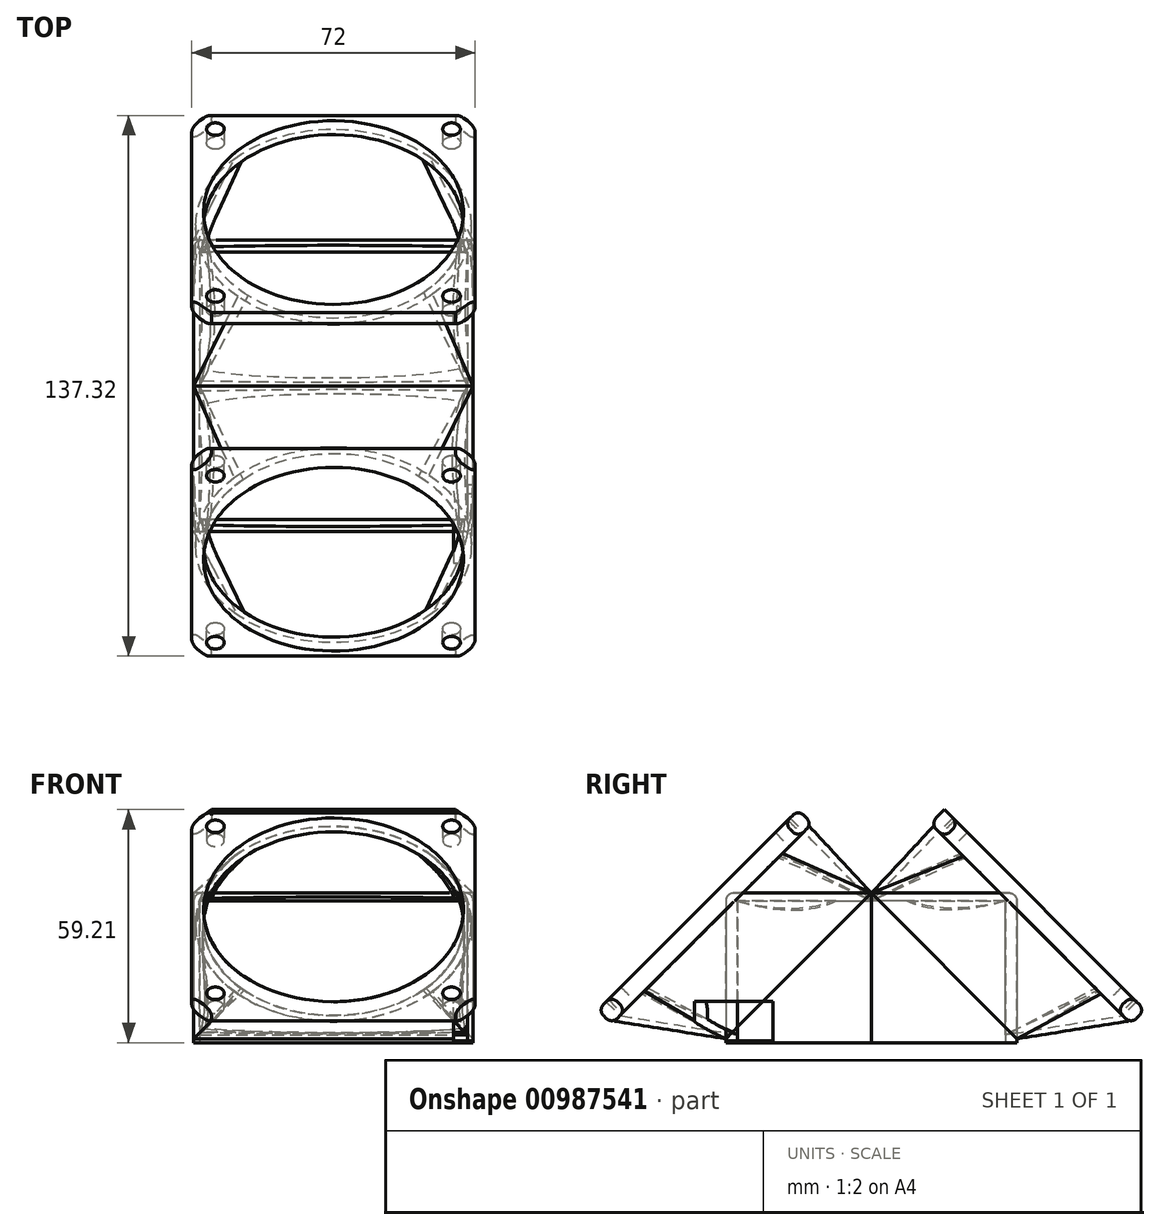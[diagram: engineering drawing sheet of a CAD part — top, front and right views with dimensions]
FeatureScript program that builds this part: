
annotation { "Feature Type Name" : "Feature", "Feature Type Description" : "" }
export const myFeature = defineFeature(function(context is Context, id is Id, definition is map)
    precondition{}
    {
        {
            var Q0;
            Q0=qCreatedBy(makeId("Front.planeOp"),FACE);
            var sketch = newSketch(context, id + "F0", { "sketchPlane" : qUnion([Q0])});
            skLineSegment(sketch, "E0.bottom", {"start": v(-34, 18) * mm, "end": v(34, 18) * mm});
            skLineSegment(sketch, "E0.top", {"start": v(-34, -18) * mm, "end": v(34, -18) * mm});
            skLineSegment(sketch, "E0.left", {"start": v(-34, 18) * mm, "end": v(-34, -18) * mm});
            skLineSegment(sketch, "E0.right", {"start": v(34, 18) * mm, "end": v(34, -18) * mm});
            skPoint(sketch, "E0.middle", {"position": v(0, 0) * mm});
            skSolve(sketch);
        }
        {
            var Q0;
            Q0=makeQuery(id+"F0.imprint","IMPRINT",FACE,{"disambiguationData":[TD([[makeQuery(id+"F0.imprint","IMPRINT",EDGE,{"derivedFrom":sQuery(id+"F0.wireOp",EDGE,"E0.bottom")}),-1.0]])]});
            extrude(context, id + "F1", {"entities" : qUnion([Q0]), "depth" : 34 * mm, "offsetDistance" : 25 * mm});
        }
        {
            var Q0;
            Q0=makeQuery(id+"F1.opExtrude","CAP_FACE",FACE,{"disambiguationData":[OSD([sQuery(id+"F0.wireOp",EDGE,"E0.bottom"),sQuery(id+"F0.wireOp",EDGE,"E0.top"),sQuery(id+"F0.wireOp",EDGE,"E0.left"),sQuery(id+"F0.wireOp",EDGE,"E0.right")])],"isStart":false});
            var sketch = newSketch(context, id + "F2", { "sketchPlane" : qUnion([Q0])});
            skLineSegment(sketch, "E1", {"start": v(-34, 0) * mm, "end": v(34, 0) * mm, "construction": true});
            skSolve(sketch);
        }
        {
            var Q0;
            Q0=sQuery(id+"F0.wireOp",EDGE,"E0.top");
            cPlane(context, id + "F3", {"entities" : qUnion([Q0]), "cplaneType" : CPlaneType.LINE_ANGLE, "offset" : 25 * mm, "angle" : 45 * degree, "oppositeDirection" : true, "width" : 150 * mm, "height" : 150 * mm});
        }
        {
            var Q0;
            Q0=sQuery(id+"F0.wireOp",EDGE,"E0.bottom");
            cPlane(context, id + "F4", {"entities" : qUnion([Q0]), "cplaneType" : CPlaneType.LINE_ANGLE, "offset" : 25 * mm, "angle" : 45 * degree, "oppositeDirection" : true, "width" : 150 * mm, "height" : 150 * mm});
        }
        {
            var Q0;
            Q0=qCreatedBy(id+"F4.planeOp",FACE);
            var sketch = newSketch(context, id + "F5", { "sketchPlane" : qUnion([Q0])});
            skLineSegment(sketch, "E2.bottom", {"start": v(-34, 12.73) * mm, "end": v(34, 12.73) * mm});
            skLineSegment(sketch, "E2.top", {"start": v(-34, -35.36) * mm, "end": v(34, -35.36) * mm});
            skLineSegment(sketch, "E2.left", {"start": v(-34, 12.73) * mm, "end": v(-34, -35.36) * mm});
            skLineSegment(sketch, "E2.right", {"start": v(34, 12.73) * mm, "end": v(34, -35.36) * mm});
            skSolve(sketch);
        }
        {
            var Q0;
            Q0=qCreatedBy(id+"F3.planeOp",FACE);
            cPlane(context, id + "F6", {"entities" : qUnion([Q0]), "cplaneType" : CPlaneType.OFFSET, "offset" : 50 * mm, "oppositeDirection" : true, "width" : 150 * mm, "height" : 150 * mm});
        }
        {
            var Q0;
            Q0=qCreatedBy(id+"F6.planeOp",FACE);
            var sketch = newSketch(context, id + "F7", { "sketchPlane" : qUnion([Q0])});
            skArc(sketch, "E3", {"start": v(22.98, 3.69) * mm, "mid": v(0.9, 12.99) * mm, "end": v(-21.64, 4.91) * mm});
            skArc(sketch, "E4", {"start": v(-21.64, 4.91) * mm, "mid": v(-32.97, -18.7) * mm, "end": v(-23.53, -43.14) * mm});
            skArc(sketch, "E5", {"start": v(-23.53, -43.14) * mm, "mid": v(-0.57, -53) * mm, "end": v(22.72, -43.93) * mm});
            skArc(sketch, "E6", {"start": v(22.72, -43.93) * mm, "mid": v(33, -20.18) * mm, "end": v(22.98, 3.69) * mm});
            skSolve(sketch);
        }
        {
            var Q0;
            Q0=qSketchRegion(id+"F5",true);
            var Q1;
            Q1=makeQuery(id+"F7.imprint","IMPRINT",FACE,{"disambiguationData":[TD([[makeQuery(id+"F7.imprint","IMPRINT",EDGE,{"derivedFrom":sQuery(id+"F7.wireOp",EDGE,"E3")}),1.0]])]});
            loft(context, id + "F8", {"sheetProfilesArray" : [{ "sheetProfileEntities" : qUnion([Q0]) }, { "sheetProfileEntities" : qUnion([Q1]) }]});
        }
        {
            var Q0;
            Q0=makeQuery(id+"F0.imprint","IMPRINT",FACE,{"disambiguationData":[TD([[makeQuery(id+"F0.imprint","IMPRINT",EDGE,{"derivedFrom":sQuery(id+"F0.wireOp",EDGE,"E0.bottom")}),-1.0]])]});
            var sketch = newSketch(context, id + "F9", { "sketchPlane" : qUnion([Q0])});
            skLineSegment(sketch, "E7", {"start": v(0, 18) * mm, "end": v(0, -18) * mm, "construction": true});
            skSolve(sketch);
        }
        {
            var Q0;
            Q0=makeQuery(id+"F9.imprint","IMPRINT",FACE,{"disambiguationData":[TD([[makeQuery(id+"F9.imprint","IMPRINT",EDGE,{"derivedFrom":makeQuery(id+"F0.imprint","IMPRINT",EDGE,{"derivedFrom":sQuery(id+"F0.wireOp",EDGE,"E0.bottom")})}),-1.0]])]});
            var sketch = newSketch(context, id + "F10", { "sketchPlane" : qUnion([Q0])});
            skLineSegment(sketch, "E8.bottom", {"start": v(35.5, 20) * mm, "end": v(-35.5, 20) * mm});
            skLineSegment(sketch, "E8.top", {"start": v(35.5, -18) * mm, "end": v(-35.5, -18) * mm});
            skLineSegment(sketch, "E8.left", {"start": v(35.5, 20) * mm, "end": v(35.5, -18) * mm});
            skLineSegment(sketch, "E8.right", {"start": v(-35.5, 20) * mm, "end": v(-35.5, -18) * mm});
            skPoint(sketch, "E8.middle", {"position": v(0, 0) * mm});
            skSolve(sketch);
        }
        {
            var Q0;
            Q0=qSketchRegion(id+"F10",true);
            extrude(context, id + "F11", {"entities" : qUnion([Q0]), "depth" : 37 * mm, "offsetDistance" : 25 * mm});
        }
        {
            var Q0;
            Q0=sQuery(id+"F10.wireOp",EDGE,"E8.bottom");
            cPlane(context, id + "F12", {"entities" : qUnion([Q0]), "cplaneType" : CPlaneType.LINE_ANGLE, "offset" : 25 * mm, "angle" : 45 * degree, "width" : 150 * mm, "height" : 150 * mm});
        }
        {
            var Q0;
            Q0=qCreatedBy(id+"F12.planeOp",FACE);
            var sketch = newSketch(context, id + "F13", { "sketchPlane" : qUnion([Q0])});
            skLineSegment(sketch, "E9.bottom", {"start": v(-35.5, 14.14) * mm, "end": v(35.5, 14.14) * mm});
            skLineSegment(sketch, "E9.top", {"start": v(-35.5, -38.18) * mm, "end": v(35.5, -38.18) * mm});
            skLineSegment(sketch, "E9.left", {"start": v(-35.5, 14.14) * mm, "end": v(-35.5, -38.18) * mm});
            skLineSegment(sketch, "E9.right", {"start": v(35.5, 14.14) * mm, "end": v(35.5, -38.18) * mm});
            skSolve(sketch);
        }
        {
            var Q0;
            Q0=qCreatedBy(id+"F6.planeOp",FACE);
            var sketch = newSketch(context, id + "F14", { "sketchPlane" : qUnion([Q0])});
            skCircle(sketch, "E10", {"center": v(0, -20) * mm, "radius": 35 * mm});
            skSolve(sketch);
        }
        {
            var Q0;
            Q0=qCreatedBy(id+"F6.planeOp",FACE);
            var sketch = newSketch(context, id + "F15", { "sketchPlane" : qUnion([Q0])});
            skLineSegment(sketch, "E11.bottom", {"start": v(-36, -56) * mm, "end": v(36, -56) * mm});
            skLineSegment(sketch, "E11.top", {"start": v(-36, 16) * mm, "end": v(36, 16) * mm});
            skLineSegment(sketch, "E11.left", {"start": v(-36, -56) * mm, "end": v(-36, 16) * mm});
            skLineSegment(sketch, "E11.right", {"start": v(36, -56) * mm, "end": v(36, 16) * mm});
            skPoint(sketch, "E11.middle", {"position": v(0, -20) * mm});
            skSolve(sketch);
        }
        {
            var Q0;
            Q0=qCreatedBy(id+"F6.planeOp",FACE);
            var sketch = newSketch(context, id + "F16", { "sketchPlane" : qUnion([Q0])});
            skLineSegment(sketch, "E12.bottom", {"start": v(-30, -50) * mm, "end": v(30, -50) * mm, "construction": true});
            skLineSegment(sketch, "E12.top", {"start": v(-30, 10) * mm, "end": v(30, 10) * mm, "construction": true});
            skLineSegment(sketch, "E12.left", {"start": v(-30, -50) * mm, "end": v(-30, 10) * mm, "construction": true});
            skLineSegment(sketch, "E12.right", {"start": v(30, -50) * mm, "end": v(30, 10) * mm, "construction": true});
            skPoint(sketch, "E12.middle", {"position": v(0, -20) * mm});
            skSolve(sketch);
        }
        {
            var Q0;
            Q0=qCreatedBy(id+"F6.planeOp",FACE);
            var sketch = newSketch(context, id + "F17", { "sketchPlane" : qUnion([Q0])});
            skCircle(sketch, "E13", {"center": v(30, -50) * mm, "radius": 2.25 * mm});
            skCircle(sketch, "E14", {"center": v(-30, -50) * mm, "radius": 2.25 * mm});
            skCircle(sketch, "E15", {"center": v(-30, 10) * mm, "radius": 2.25 * mm});
            skCircle(sketch, "E16", {"center": v(30, 10) * mm, "radius": 2.25 * mm});
            skSolve(sketch);
        }
        {
            var Q0;
            Q0=makeQuery(id+"F8.opLoft","CAP_FACE",FACE,{"disambiguationData":[OSD([makeQuery(id+"F7.imprint","IMPRINT",FACE,{"disambiguationData":[TD([[makeQuery(id+"F7.imprint","IMPRINT",EDGE,{"derivedFrom":sQuery(id+"F7.wireOp",EDGE,"E3")}),1.0]])]})])],"isStart":true});
            var Q1;
            Q1=makeQuery(id+"F17.imprint","IMPRINT",FACE,{"disambiguationData":[TD([[makeQuery(id+"F17.imprint","IMPRINT",EDGE,{"derivedFrom":sQuery(id+"F17.wireOp",EDGE,"E16")}),1.0]])]});
            var Q2;
            Q2=makeQuery(id+"F17.imprint","IMPRINT",FACE,{"disambiguationData":[TD([[makeQuery(id+"F17.imprint","IMPRINT",EDGE,{"derivedFrom":sQuery(id+"F17.wireOp",EDGE,"E15")}),1.0]])]});
            var Q3;
            Q3=makeQuery(id+"F17.imprint","IMPRINT",FACE,{"disambiguationData":[TD([[makeQuery(id+"F17.imprint","IMPRINT",EDGE,{"derivedFrom":sQuery(id+"F17.wireOp",EDGE,"E14")}),1.0]])]});
            var Q4;
            Q4=makeQuery(id+"F17.imprint","IMPRINT",FACE,{"disambiguationData":[TD([[makeQuery(id+"F17.imprint","IMPRINT",EDGE,{"derivedFrom":sQuery(id+"F17.wireOp",EDGE,"E13")}),1.0]])]});
            extrude(context, id + "F18", {"entities" : qUnion([Q0, Q1, Q2, Q3, Q4]), "depth" : 5 * mm, "offsetDistance" : 25 * mm});
        }
        {
            var Q0;
            Q0=makeQuery(id+"F13.imprint","IMPRINT",FACE,{"disambiguationData":[TD([[makeQuery(id+"F13.imprint","IMPRINT",EDGE,{"derivedFrom":sQuery(id+"F13.wireOp",EDGE,"E9.bottom")}),-1.0]])]});
            var Q1;
            Q1=qSketchRegion(id+"F14",true);
            loft(context, id + "F19", {"sheetProfilesArray" : [{ "sheetProfileEntities" : qUnion([Q0]) }, { "sheetProfileEntities" : qUnion([Q1]) }]});
        }
        {
            var Q0;
            Q0=makeQuery(id+"F15.imprint","IMPRINT",FACE,{"disambiguationData":[TD([[makeQuery(id+"F15.imprint","IMPRINT",EDGE,{"derivedFrom":sQuery(id+"F15.wireOp",EDGE,"E11.bottom")}),1.0]])]});
            extrude(context, id + "F20", {"entities" : qUnion([Q0]), "oppositeDirection" : true, "depth" : 5 * mm, "offsetDistance" : 25 * mm});
        }
        {
            var Q0;
            Q0=makeQuery(id+"F18.opExtrude","SWEPT_BODY",BODY,{"disambiguationData":[OSD([sQuery(id+"F17.wireOp",EDGE,"E16")])]});
            var Q1;
            Q1=makeQuery(id+"F18.opExtrude","SWEPT_BODY",BODY,{"disambiguationData":[OSD([sQuery(id+"F17.wireOp",EDGE,"E15")])]});
            var Q2;
            Q2=makeQuery(id+"F18.opExtrude","SWEPT_BODY",BODY,{"disambiguationData":[OSD([sQuery(id+"F17.wireOp",EDGE,"E14")])]});
            var Q3;
            Q3=makeQuery(id+"F18.opExtrude","SWEPT_BODY",BODY,{"disambiguationData":[OSD([sQuery(id+"F17.wireOp",EDGE,"E13")])]});
            var Q4;
            Q4=makeQuery(id+"F18.opExtrude","SWEPT_BODY",BODY,{"disambiguationData":[OSD([makeQuery(id+"F7.imprint","IMPRINT",FACE,{"disambiguationData":[TD([[makeQuery(id+"F7.imprint","IMPRINT",EDGE,{"derivedFrom":sQuery(id+"F7.wireOp",EDGE,"E3")}),1.0]])]})])]});
            var Q5;
            Q5=makeQuery(id+"F8.opLoft","SWEPT_BODY",BODY,{"disambiguationData":[OSD([makeQuery(id+"F5.imprint","IMPRINT",FACE,{"disambiguationData":[TD([[makeQuery(id+"F5.imprint","IMPRINT",EDGE,{"derivedFrom":sQuery(id+"F5.wireOp",EDGE,"E2.bottom")}),-1.0]])]}),makeQuery(id+"F7.imprint","IMPRINT",FACE,{"disambiguationData":[TD([[makeQuery(id+"F7.imprint","IMPRINT",EDGE,{"derivedFrom":sQuery(id+"F7.wireOp",EDGE,"E3")}),1.0]])]})])]});
            var Q6;
            Q6=makeQuery(id+"F1.opExtrude","SWEPT_BODY",BODY,{"disambiguationData":[OSD([sQuery(id+"F0.wireOp",EDGE,"E0.bottom"),sQuery(id+"F0.wireOp",EDGE,"E0.top"),sQuery(id+"F0.wireOp",EDGE,"E0.left"),sQuery(id+"F0.wireOp",EDGE,"E0.right")])]});
            var Q7;
            Q7=makeQuery(id+"F11.opExtrude","SWEPT_BODY",BODY,{"disambiguationData":[OSD([sQuery(id+"F10.wireOp",EDGE,"E8.bottom"),sQuery(id+"F10.wireOp",EDGE,"E8.top"),sQuery(id+"F10.wireOp",EDGE,"E8.left"),sQuery(id+"F10.wireOp",EDGE,"E8.right")])]});
            var Q8;
            Q8=makeQuery(id+"F19.opLoft","SWEPT_BODY",BODY,{"disambiguationData":[OSD([makeQuery(id+"F13.imprint","IMPRINT",FACE,{"disambiguationData":[TD([[makeQuery(id+"F13.imprint","IMPRINT",EDGE,{"derivedFrom":sQuery(id+"F13.wireOp",EDGE,"E9.bottom")}),-1.0]])]}),makeQuery(id+"F14.imprint","IMPRINT",FACE,{"disambiguationData":[TD([[makeQuery(id+"F14.imprint","IMPRINT",EDGE,{"derivedFrom":sQuery(id+"F14.wireOp",EDGE,"E10")}),1.0]])]})])]});
            var Q9;
            Q9=makeQuery(id+"F20.opExtrude","SWEPT_BODY",BODY,{"disambiguationData":[OSD([sQuery(id+"F15.wireOp",EDGE,"E11.bottom"),sQuery(id+"F15.wireOp",EDGE,"E11.top"),sQuery(id+"F15.wireOp",EDGE,"E11.left"),sQuery(id+"F15.wireOp",EDGE,"E11.right")])]});
            booleanBodies(context, id + "F21", {"operationType" : BooleanOperationType.SUBTRACTION, "tools" : qUnion([Q0, Q1, Q2, Q3, Q4, Q5, Q6]), "targets" : qUnion([Q7, Q8, Q9])});
        }
        {
            var Q0;
            Q0=makeQuery(id+"F11.opExtrude","SWEPT_BODY",BODY,{"disambiguationData":[OSD([sQuery(id+"F10.wireOp",EDGE,"E8.bottom"),sQuery(id+"F10.wireOp",EDGE,"E8.top"),sQuery(id+"F10.wireOp",EDGE,"E8.left"),sQuery(id+"F10.wireOp",EDGE,"E8.right")])]});
            var Q1;
            Q1=sQuery(id+"F9.wireOp",EDGE,"E7");
            transform(context, id + "F22", {"entities" : qUnion([Q0]), "transformType" : TransformType.ROTATION, "transformAxis" : qUnion([Q1]), "angle" : 180 * degree, "makeCopy" : true});
        }
        {
            var Q0;
            Q0=makeQuery(id+"F19.opLoft","SWEPT_BODY",BODY,{"disambiguationData":[OSD([makeQuery(id+"F13.imprint","IMPRINT",FACE,{"disambiguationData":[TD([[makeQuery(id+"F13.imprint","IMPRINT",EDGE,{"derivedFrom":sQuery(id+"F13.wireOp",EDGE,"E9.bottom")}),-1.0]])]}),makeQuery(id+"F14.imprint","IMPRINT",FACE,{"disambiguationData":[TD([[makeQuery(id+"F14.imprint","IMPRINT",EDGE,{"derivedFrom":sQuery(id+"F14.wireOp",EDGE,"E10")}),1.0]])]})])]});
            var Q1;
            Q1=sQuery(id+"F9.wireOp",EDGE,"E7");
            transform(context, id + "F23", {"entities" : qUnion([Q0]), "transformType" : TransformType.ROTATION, "transformAxis" : qUnion([Q1]), "angle" : 180 * degree, "makeCopy" : true});
        }
        {
            var Q0;
            Q0=makeQuery(id+"F20.opExtrude","SWEPT_BODY",BODY,{"disambiguationData":[OSD([sQuery(id+"F15.wireOp",EDGE,"E11.bottom"),sQuery(id+"F15.wireOp",EDGE,"E11.top"),sQuery(id+"F15.wireOp",EDGE,"E11.left"),sQuery(id+"F15.wireOp",EDGE,"E11.right")])]});
            var Q1;
            Q1=sQuery(id+"F9.wireOp",EDGE,"E7");
            transform(context, id + "F24", {"entities" : qUnion([Q0]), "transformType" : TransformType.ROTATION, "transformAxis" : qUnion([Q1]), "angle" : 180 * degree, "makeCopy" : true});
        }
        {
            var Q0;
            Q0=makeQuery(id+"F20.opExtrude","SWEPT_EDGE",EDGE,{"disambiguationData":[OSD([sQuery(id+"F15.wireOp",EDGE,"E11.bottom"),sQuery(id+"F15.wireOp",EDGE,"E11.left")])]});
            var Q1;
            Q1=makeQuery(id+"F20.opExtrude","SWEPT_EDGE",EDGE,{"disambiguationData":[OSD([sQuery(id+"F15.wireOp",EDGE,"E11.bottom"),sQuery(id+"F15.wireOp",EDGE,"E11.right")])]});
            var Q2;
            Q2=makeQuery(id+"F20.opExtrude","SWEPT_EDGE",EDGE,{"disambiguationData":[OSD([sQuery(id+"F15.wireOp",EDGE,"E11.top"),sQuery(id+"F15.wireOp",EDGE,"E11.left")])]});
            var Q3;
            Q3=makeQuery(id+"F20.opExtrude","SWEPT_EDGE",EDGE,{"disambiguationData":[OSD([sQuery(id+"F15.wireOp",EDGE,"E11.top"),sQuery(id+"F15.wireOp",EDGE,"E11.right")])]});
            var Q4;
            Q4=makeQuery(id+"F24.opPattern","COPY",EDGE,{"derivedFrom":makeQuery(id+"F20.opExtrude","SWEPT_EDGE",EDGE,{"disambiguationData":[OSD([sQuery(id+"F15.wireOp",EDGE,"E11.top"),sQuery(id+"F15.wireOp",EDGE,"E11.left")])]}),"instanceName":"1"});
            var Q5;
            Q5=makeQuery(id+"F24.opPattern","COPY",EDGE,{"derivedFrom":makeQuery(id+"F20.opExtrude","SWEPT_EDGE",EDGE,{"disambiguationData":[OSD([sQuery(id+"F15.wireOp",EDGE,"E11.top"),sQuery(id+"F15.wireOp",EDGE,"E11.right")])]}),"instanceName":"1"});
            var Q6;
            Q6=makeQuery(id+"F24.opPattern","COPY",EDGE,{"derivedFrom":makeQuery(id+"F20.opExtrude","SWEPT_EDGE",EDGE,{"disambiguationData":[OSD([sQuery(id+"F15.wireOp",EDGE,"E11.bottom"),sQuery(id+"F15.wireOp",EDGE,"E11.left")])]}),"instanceName":"1"});
            var Q7;
            Q7=makeQuery(id+"F24.opPattern","COPY",EDGE,{"derivedFrom":makeQuery(id+"F20.opExtrude","SWEPT_EDGE",EDGE,{"disambiguationData":[OSD([sQuery(id+"F15.wireOp",EDGE,"E11.bottom"),sQuery(id+"F15.wireOp",EDGE,"E11.right")])]}),"instanceName":"1"});
            chamfer(context, id + "F25", {"entities" : qUnion([Q0, Q1, Q2, Q3, Q4, Q5, Q6, Q7]), "width" : 5 * mm, "tangentPropagation" : true});
        }
        {
            var Q0;
            Q0=makeQuery(id+"F20.opExtrude","CAP_EDGE",EDGE,{"disambiguationData":[OSD([sQuery(id+"F15.wireOp",EDGE,"E11.left")])],"isStart":false});
            var Q1;
            Q1=makeQuery(id+"F20.opExtrude","CAP_EDGE",EDGE,{"disambiguationData":[OSD([sQuery(id+"F15.wireOp",EDGE,"E11.top")])],"isStart":false});
            var Q2;
            Q2=makeQuery(id+"F20.opExtrude","CAP_EDGE",EDGE,{"disambiguationData":[OSD([sQuery(id+"F15.wireOp",EDGE,"E11.right")])],"isStart":false});
            var Q3;
            Q3=makeQuery(id+"F20.opExtrude","CAP_EDGE",EDGE,{"disambiguationData":[OSD([sQuery(id+"F15.wireOp",EDGE,"E11.bottom")])],"isStart":false});
            var Q4;
            Q4=makeQuery(id+"F20.opExtrude","CAP_EDGE",EDGE,{"disambiguationData":[OSD([sQuery(id+"F15.wireOp",EDGE,"E11.left")])],"isStart":true});
            var Q5;
            Q5=makeQuery(id+"F20.opExtrude","CAP_EDGE",EDGE,{"disambiguationData":[OSD([sQuery(id+"F15.wireOp",EDGE,"E11.bottom")])],"isStart":true});
            var Q6;
            Q6=makeQuery(id+"F20.opExtrude","CAP_EDGE",EDGE,{"disambiguationData":[OSD([sQuery(id+"F15.wireOp",EDGE,"E11.right")])],"isStart":true});
            var Q7;
            Q7=makeQuery(id+"F20.opExtrude","CAP_EDGE",EDGE,{"disambiguationData":[OSD([sQuery(id+"F15.wireOp",EDGE,"E11.top")])],"isStart":true});
            var Q8;
            Q8=makeQuery(id+"F11.opExtrude","CAP_EDGE",EDGE,{"disambiguationData":[OSD([sQuery(id+"F10.wireOp",EDGE,"E8.right")])],"isStart":false});
            var Q9;
            {var subQ0=sQuery(id+"F10.wireOp",EDGE,"E8.bottom");var subQ1=sQuery(id+"F10.wireOp",EDGE,"E8.right");Q9=makeQuery(id+"F21.opBoolean","SPLIT",EDGE,{"disambiguationData":[TD([makeQuery(id+"F11.opExtrude","SWEPT_FACE",FACE,{"disambiguationData":[OSD([subQ1])]})])],"derivedFrom":makeQuery(id+"F11.opExtrude","CAP_EDGE",EDGE,{"disambiguationData":[OSD([subQ0])],"isStart":false})});}
            var Q10;
            Q10=makeQuery(id+"F11.opExtrude","SWEPT_EDGE",EDGE,{"disambiguationData":[OSD([sQuery(id+"F10.wireOp",EDGE,"E8.bottom"),sQuery(id+"F10.wireOp",EDGE,"E8.right")])]});
            var Q11;
            Q11=makeQuery(id+"F11.opExtrude","CAP_EDGE",EDGE,{"disambiguationData":[OSD([sQuery(id+"F10.wireOp",EDGE,"E8.left")])],"isStart":false});
            var Q12;
            Q12=makeQuery(id+"F11.opExtrude","SWEPT_EDGE",EDGE,{"disambiguationData":[OSD([sQuery(id+"F10.wireOp",EDGE,"E8.bottom"),sQuery(id+"F10.wireOp",EDGE,"E8.left")])]});
            var Q13;
            {var subQ0=sQuery(id+"F10.wireOp",EDGE,"E8.bottom");var subQ1=sQuery(id+"F10.wireOp",EDGE,"E8.left");Q13=makeQuery(id+"F21.opBoolean","SPLIT",EDGE,{"disambiguationData":[TD([makeQuery(id+"F11.opExtrude","SWEPT_FACE",FACE,{"disambiguationData":[OSD([subQ1])]})])],"derivedFrom":makeQuery(id+"F11.opExtrude","CAP_EDGE",EDGE,{"disambiguationData":[OSD([subQ0])],"isStart":false})});}
            var Q14;
            Q14=makeQuery(id+"F22.opPattern","COPY",EDGE,{"derivedFrom":makeQuery(id+"F11.opExtrude","SWEPT_EDGE",EDGE,{"disambiguationData":[OSD([sQuery(id+"F10.wireOp",EDGE,"E8.bottom"),sQuery(id+"F10.wireOp",EDGE,"E8.right")])]}),"instanceName":"1"});
            var Q15;
            {var subQ0=sQuery(id+"F10.wireOp",EDGE,"E8.bottom");var subQ1=sQuery(id+"F10.wireOp",EDGE,"E8.right");Q15=makeQuery(id+"F22.opPattern","COPY",EDGE,{"derivedFrom":makeQuery(id+"F21.opBoolean","SPLIT",EDGE,{"disambiguationData":[TD([makeQuery(id+"F11.opExtrude","SWEPT_FACE",FACE,{"disambiguationData":[OSD([subQ1])]})])],"derivedFrom":makeQuery(id+"F11.opExtrude","CAP_EDGE",EDGE,{"disambiguationData":[OSD([subQ0])],"isStart":false})}),"instanceName":"1"});}
            var Q16;
            Q16=makeQuery(id+"F22.opPattern","COPY",EDGE,{"derivedFrom":makeQuery(id+"F11.opExtrude","CAP_EDGE",EDGE,{"disambiguationData":[OSD([sQuery(id+"F10.wireOp",EDGE,"E8.right")])],"isStart":false}),"instanceName":"1"});
            var Q17;
            Q17=makeQuery(id+"F24.opPattern","COPY",EDGE,{"derivedFrom":makeQuery(id+"F20.opExtrude","CAP_EDGE",EDGE,{"disambiguationData":[OSD([sQuery(id+"F15.wireOp",EDGE,"E11.right")])],"isStart":false}),"instanceName":"1"});
            var Q18;
            Q18=makeQuery(id+"F24.opPattern","COPY",EDGE,{"derivedFrom":makeQuery(id+"F20.opExtrude","CAP_EDGE",EDGE,{"disambiguationData":[OSD([sQuery(id+"F15.wireOp",EDGE,"E11.right")])],"isStart":true}),"instanceName":"1"});
            var Q19;
            Q19=makeQuery(id+"F24.opPattern","COPY",EDGE,{"derivedFrom":makeQuery(id+"F20.opExtrude","CAP_EDGE",EDGE,{"disambiguationData":[OSD([sQuery(id+"F15.wireOp",EDGE,"E11.top")])],"isStart":true}),"instanceName":"1"});
            var Q20;
            Q20=makeQuery(id+"F24.opPattern","COPY",EDGE,{"derivedFrom":makeQuery(id+"F20.opExtrude","CAP_EDGE",EDGE,{"disambiguationData":[OSD([sQuery(id+"F15.wireOp",EDGE,"E11.bottom")])],"isStart":true}),"instanceName":"1"});
            var Q21;
            Q21=makeQuery(id+"F24.opPattern","COPY",EDGE,{"derivedFrom":makeQuery(id+"F20.opExtrude","CAP_EDGE",EDGE,{"disambiguationData":[OSD([sQuery(id+"F15.wireOp",EDGE,"E11.bottom")])],"isStart":false}),"instanceName":"1"});
            var Q22;
            Q22=makeQuery(id+"F24.opPattern","COPY",EDGE,{"derivedFrom":makeQuery(id+"F20.opExtrude","CAP_EDGE",EDGE,{"disambiguationData":[OSD([sQuery(id+"F15.wireOp",EDGE,"E11.left")])],"isStart":false}),"instanceName":"1"});
            var Q23;
            Q23=makeQuery(id+"F24.opPattern","COPY",EDGE,{"derivedFrom":makeQuery(id+"F20.opExtrude","CAP_EDGE",EDGE,{"disambiguationData":[OSD([sQuery(id+"F15.wireOp",EDGE,"E11.left")])],"isStart":true}),"instanceName":"1"});
            var Q24;
            Q24=makeQuery(id+"F22.opPattern","COPY",EDGE,{"derivedFrom":makeQuery(id+"F11.opExtrude","CAP_EDGE",EDGE,{"disambiguationData":[OSD([sQuery(id+"F10.wireOp",EDGE,"E8.left")])],"isStart":false}),"instanceName":"1"});
            var Q25;
            {var subQ0=sQuery(id+"F10.wireOp",EDGE,"E8.bottom");var subQ1=sQuery(id+"F10.wireOp",EDGE,"E8.left");Q25=makeQuery(id+"F22.opPattern","COPY",EDGE,{"derivedFrom":makeQuery(id+"F21.opBoolean","SPLIT",EDGE,{"disambiguationData":[TD([makeQuery(id+"F11.opExtrude","SWEPT_FACE",FACE,{"disambiguationData":[OSD([subQ1])]})])],"derivedFrom":makeQuery(id+"F11.opExtrude","CAP_EDGE",EDGE,{"disambiguationData":[OSD([subQ0])],"isStart":false})}),"instanceName":"1"});}
            var Q26;
            Q26=makeQuery(id+"F22.opPattern","COPY",EDGE,{"derivedFrom":makeQuery(id+"F11.opExtrude","SWEPT_EDGE",EDGE,{"disambiguationData":[OSD([sQuery(id+"F10.wireOp",EDGE,"E8.bottom"),sQuery(id+"F10.wireOp",EDGE,"E8.left")])]}),"instanceName":"1"});
            fillet(context, id + "F26", {"entities" : qUnion([Q0, Q1, Q2, Q3, Q4, Q5, Q6, Q7, Q8, Q9, Q10, Q11, Q12, Q13, Q14, Q15, Q16, Q17, Q18, Q19, Q20, Q21, Q22, Q23, Q24, Q25, Q26]), "radius" : 2 * mm, "tangentPropagation" : true, "allowEdgeOverflow" : false});
        }
        {
            var Q0;
            Q0=makeQuery(id+"F11.opExtrude","SWEPT_FACE",FACE,{"disambiguationData":[OSD([sQuery(id+"F10.wireOp",EDGE,"E8.left")])]});
            var sketch = newSketch(context, id + "F27", { "sketchPlane" : qUnion([Q0])});
            skLineSegment(sketch, "E17.bottom", {"start": v(-25, -17.5) * mm, "end": v(-45, -17.5) * mm});
            skLineSegment(sketch, "E17.top", {"start": v(-25, -7.5) * mm, "end": v(-45, -7.5) * mm});
            skLineSegment(sketch, "E17.left", {"start": v(-25, -17.5) * mm, "end": v(-25, -7.5) * mm});
            skLineSegment(sketch, "E17.right", {"start": v(-45, -17.5) * mm, "end": v(-45, -7.5) * mm});
            skSolve(sketch);
        }
        {
            var Q0;
            Q0=qSketchRegion(id+"F27",true);
            extrude(context, id + "F28", {"entities" : qUnion([Q0]), "oppositeDirection" : true, "depth" : 5 * mm, "offsetDistance" : 25 * mm});
        }
        {
            var Q0;
            Q0=makeQuery(id+"F28.opExtrude","SWEPT_BODY",BODY,{"disambiguationData":[OSD([sQuery(id+"F27.wireOp",EDGE,"E17.bottom"),sQuery(id+"F27.wireOp",EDGE,"E17.top"),sQuery(id+"F27.wireOp",EDGE,"E17.left"),sQuery(id+"F27.wireOp",EDGE,"E17.right")])]});
            var Q1;
            Q1=makeQuery(id+"F11.opExtrude","SWEPT_BODY",BODY,{"disambiguationData":[OSD([sQuery(id+"F10.wireOp",EDGE,"E8.bottom"),sQuery(id+"F10.wireOp",EDGE,"E8.top"),sQuery(id+"F10.wireOp",EDGE,"E8.left"),sQuery(id+"F10.wireOp",EDGE,"E8.right")])]});
            var Q2;
            Q2=makeQuery(id+"F19.opLoft","SWEPT_BODY",BODY,{"disambiguationData":[OSD([makeQuery(id+"F13.imprint","IMPRINT",FACE,{"disambiguationData":[TD([[makeQuery(id+"F13.imprint","IMPRINT",EDGE,{"derivedFrom":sQuery(id+"F13.wireOp",EDGE,"E9.bottom")}),-1.0]])]}),makeQuery(id+"F14.imprint","IMPRINT",FACE,{"disambiguationData":[TD([[makeQuery(id+"F14.imprint","IMPRINT",EDGE,{"derivedFrom":sQuery(id+"F14.wireOp",EDGE,"E10")}),1.0]])]})])]});
            booleanBodies(context, id + "F29", {"operationType" : BooleanOperationType.SUBTRACTION, "tools" : qUnion([Q0]), "targets" : qUnion([Q1, Q2])});
        }
    });
